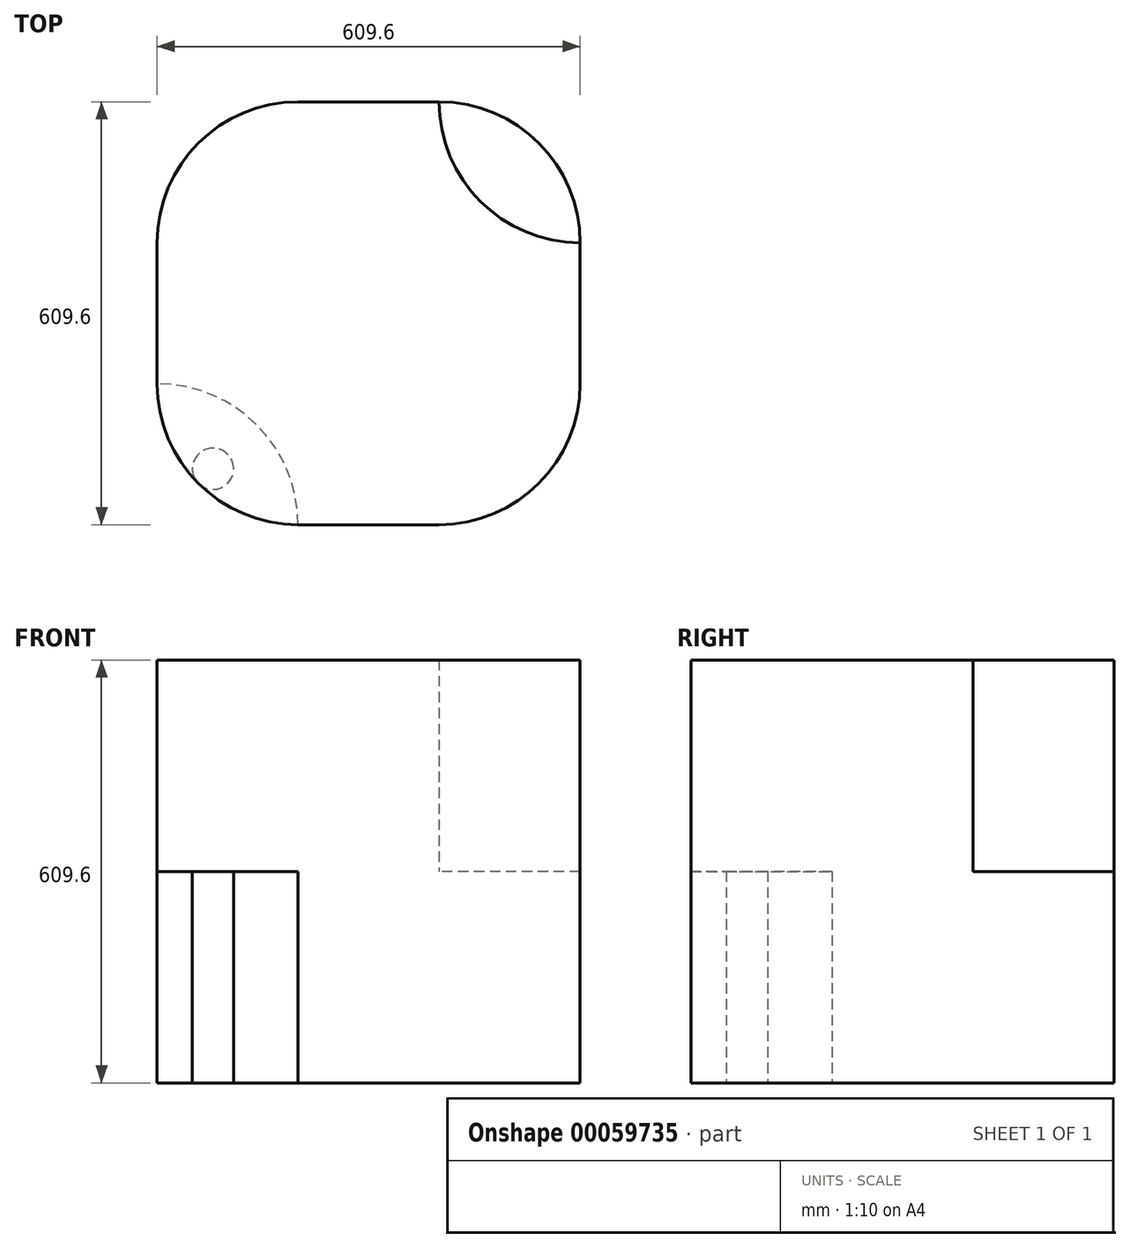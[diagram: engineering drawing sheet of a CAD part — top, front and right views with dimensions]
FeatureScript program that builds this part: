
annotation { "Feature Type Name" : "Feature", "Feature Type Description" : "" }
export const myFeature = defineFeature(function(context is Context, id is Id, definition is map)
    precondition{}
    {
        {
            var Q0;
            Q0=qCreatedBy(makeId("Top.planeOp"),FACE);
            var sketch = newSketch(context, id + "F0", { "sketchPlane" : qUnion([Q0])});
            skLineSegment(sketch, "E0.bottom", {"start": v(101.6, -304.8) * mm, "end": v(-101.6, -304.8) * mm});
            skLineSegment(sketch, "E0.top", {"start": v(101.6, 304.8) * mm, "end": v(-101.6, 304.8) * mm});
            skLineSegment(sketch, "E0.left", {"start": v(304.8, -101.6) * mm, "end": v(304.8, 101.6) * mm});
            skLineSegment(sketch, "E0.right", {"start": v(-304.8, -101.6) * mm, "end": v(-304.8, 101.6) * mm});
            skPoint(sketch, "E0.middle", {"position": v(0, 0) * mm});
            skPoint(sketch, "E1.visualSharp", {"position": v(304.8, 304.8) * mm});
            skArc(sketch, "E1.filletArc", {"start": v(304.8, 101.6) * mm, "mid": v(245.28, 245.28) * mm, "end": v(101.6, 304.8) * mm});
            skPoint(sketch, "E2.visualSharp", {"position": v(304.8, -304.8) * mm});
            skArc(sketch, "E2.filletArc", {"start": v(101.6, -304.8) * mm, "mid": v(245.28, -245.28) * mm, "end": v(304.8, -101.6) * mm});
            skPoint(sketch, "E3.visualSharp", {"position": v(-304.8, -304.8) * mm});
            skArc(sketch, "E3.filletArc", {"start": v(-304.8, -101.6) * mm, "mid": v(-245.28, -245.28) * mm, "end": v(-101.6, -304.8) * mm});
            skPoint(sketch, "E4.visualSharp", {"position": v(-304.8, 304.8) * mm});
            skArc(sketch, "E4.filletArc", {"start": v(-101.6, 304.8) * mm, "mid": v(-245.28, 245.28) * mm, "end": v(-304.8, 101.6) * mm});
            skLineSegment(sketch, "E5", {"start": v(-304.8, -101.6) * mm, "end": v(-101.6, -304.8) * mm, "construction": true});
            skLineSegment(sketch, "E6", {"start": v(101.6, 304.8) * mm, "end": v(304.8, 101.6) * mm, "construction": true});
            skArc(sketch, "E7.MirrorCS", {"start": v(304.8, 101.6) * mm, "mid": v(161.12, 161.12) * mm, "end": v(101.6, 304.8) * mm});
            skArc(sketch, "E8.MirrorCS", {"start": v(508, 711.2) * mm, "mid": v(651.68, 651.68) * mm, "end": v(711.2, 508) * mm});
            skLineSegment(sketch, "E9.MirrorCS", {"start": v(508, 711.2) * mm, "end": v(711.2, 508) * mm, "construction": true});
            skArc(sketch, "E10.MirrorCS", {"start": v(-304.8, -101.6) * mm, "mid": v(-161.12, -161.12) * mm, "end": v(-101.6, -304.8) * mm});
            skCircle(sketch, "E11", {"center": v(-224.24, -224.24) * mm, "radius": 29.76 * mm});
            skPoint(sketch, "E12", {"position": v(-161.12, -161.12) * mm});
            skLineSegment(sketch, "E13", {"start": v(-304.8, -304.8) * mm, "end": v(-101.6, -101.6) * mm, "construction": true});
            skSolve(sketch);
        }
        {
            var Q0;
            Q0=makeQuery(id+"F0.imprint","IMPRINT",FACE,{"disambiguationData":[TD([[makeQuery(id+"F0.imprint","IMPRINT",EDGE,{"derivedFrom":sQuery(id+"F0.wireOp",EDGE,"E0.bottom")}),-1.0]])]});
            var Q1;
            Q1=makeQuery(id+"F0.imprint","IMPRINT",FACE,{"disambiguationData":[TD([[makeQuery(id+"F0.imprint","IMPRINT",EDGE,{"derivedFrom":sQuery(id+"F0.wireOp",EDGE,"E1.filletArc")}),1.0]])]});
            var Q2;
            Q2=makeQuery(id+"F0.imprint","IMPRINT",FACE,{"disambiguationData":[TD([[makeQuery(id+"F0.imprint","IMPRINT",EDGE,{"derivedFrom":sQuery(id+"F0.wireOp",EDGE,"E11")}),1.0]])]});
            extrude(context, id + "F1", {"entities" : qUnion([Q0, Q1, Q2]), "depth" : 304.8 * mm});
        }
        {
            var Q0;
            Q0=makeQuery(id+"F1.opExtrude","CAP_FACE",FACE,{"disambiguationData":[OSD([sQuery(id+"F0.wireOp",EDGE,"E0.bottom"),sQuery(id+"F0.wireOp",EDGE,"E0.top"),sQuery(id+"F0.wireOp",EDGE,"E0.left"),sQuery(id+"F0.wireOp",EDGE,"E0.right"),sQuery(id+"F0.wireOp",EDGE,"E1.filletArc"),sQuery(id+"F0.wireOp",EDGE,"E2.filletArc"),sQuery(id+"F0.wireOp",EDGE,"E4.filletArc"),sQuery(id+"F0.wireOp",EDGE,"E10.MirrorCS")])],"isStart":false});
            var sketch = newSketch(context, id + "F2", { "sketchPlane" : qUnion([Q0])});
            skArc(sketch, "E14.0", {"start": v(304.8, 101.6) * mm, "mid": v(161.12, 161.12) * mm, "end": v(101.6, 304.8) * mm});
            skLineSegment(sketch, "E15.0.0", {"start": v(-101.6, -304.8) * mm, "end": v(101.6, -304.8) * mm});
            skArc(sketch, "E15.0.1", {"start": v(101.6, -304.8) * mm, "mid": v(245.28, -245.28) * mm, "end": v(304.8, -101.6) * mm});
            skLineSegment(sketch, "E15.0.2", {"start": v(304.8, -101.6) * mm, "end": v(304.8, 101.6) * mm});
            skLineSegment(sketch, "E15.0.4", {"start": v(101.6, 304.8) * mm, "end": v(-101.6, 304.8) * mm});
            skArc(sketch, "E15.0.5", {"start": v(-101.6, 304.8) * mm, "mid": v(-245.28, 245.28) * mm, "end": v(-304.8, 101.6) * mm});
            skLineSegment(sketch, "E15.0.6", {"start": v(-304.8, 101.6) * mm, "end": v(-304.8, -101.6) * mm});
            skArc(sketch, "E16.0", {"start": v(-304.8, -101.6) * mm, "mid": v(-245.28, -245.28) * mm, "end": v(-101.6, -304.8) * mm});
            skSolve(sketch);
        }
        {
            var Q0;
            Q0 = qSketchRegion(id + "F2", true);
            extrude(context, id + "F3", {"entities" : qUnion([Q0]), "operationType" : NewBodyOperationType.ADD, "depth" : 304.8 * mm});
        }
        {
            var Q0;
            Q0=makeQuery(id+"F1.opExtrude","CAP_FACE",FACE,{"disambiguationData":[OSD([sQuery(id+"F0.wireOp",EDGE,"E0.bottom"),sQuery(id+"F0.wireOp",EDGE,"E0.top"),sQuery(id+"F0.wireOp",EDGE,"E0.left"),sQuery(id+"F0.wireOp",EDGE,"E0.right"),sQuery(id+"F0.wireOp",EDGE,"E1.filletArc"),sQuery(id+"F0.wireOp",EDGE,"E2.filletArc"),sQuery(id+"F0.wireOp",EDGE,"E4.filletArc"),sQuery(id+"F0.wireOp",EDGE,"E10.MirrorCS")])],"isStart":false});
            var Q1;
            Q1=sQuery(id+"F0.wireOp",EDGE,"E1.filletArc");
            extrude(context, id + "F4", {"entities" : qUnion([Q0]), "bodyType" : ToolBodyType.SURFACE, "surfaceEntities" : qUnion([Q1]), "depth" : 406.4 * mm});
        }
    });
